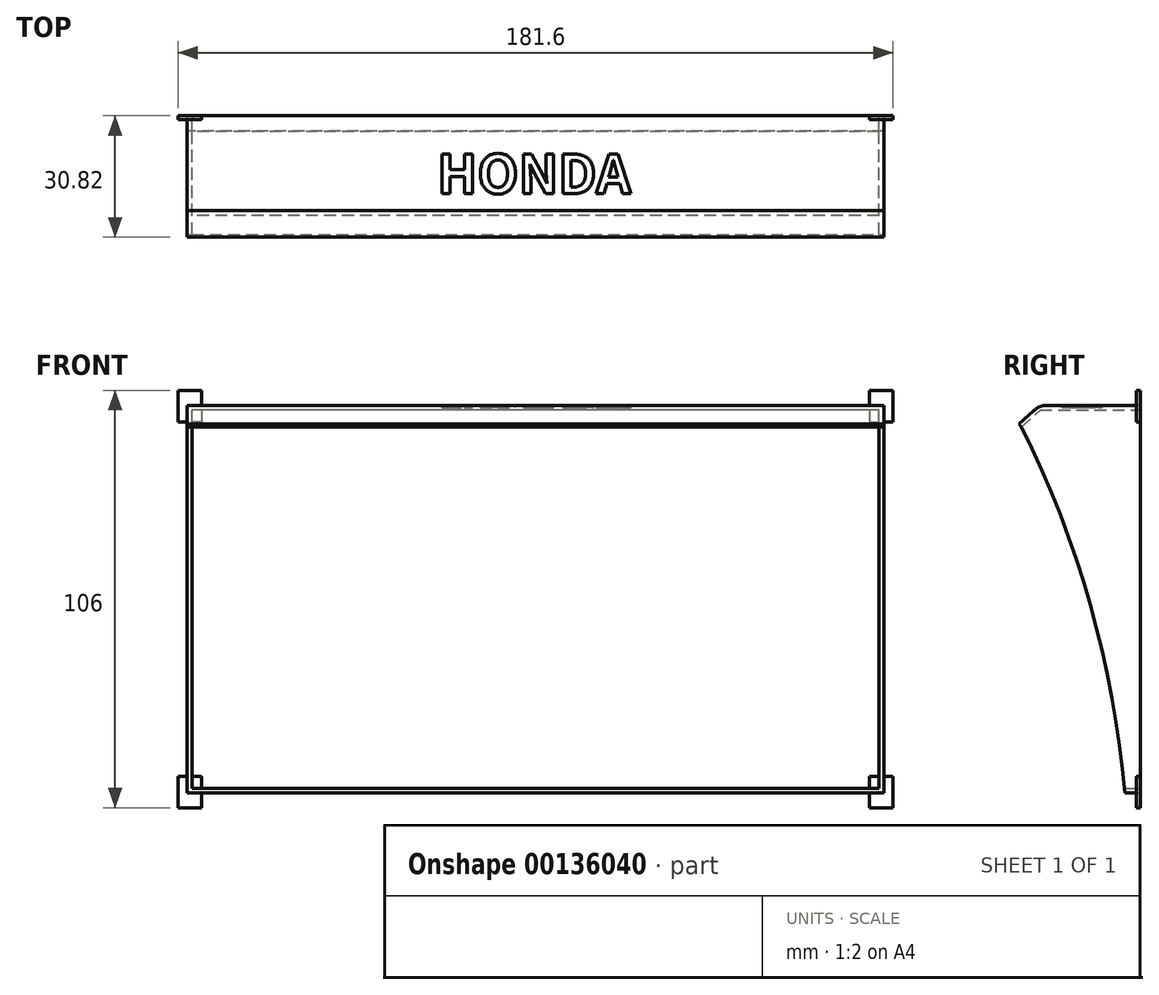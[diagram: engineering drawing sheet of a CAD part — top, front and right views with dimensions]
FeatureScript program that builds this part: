
annotation { "Feature Type Name" : "Feature", "Feature Type Description" : "" }
export const myFeature = defineFeature(function(context is Context, id is Id, definition is map)
    precondition{}
    {
        {
            var Q0;
            Q0=qCreatedBy(makeId("Front.planeOp"),FACE);
            var sketch = newSketch(context, id + "F0", { "sketchPlane" : qUnion([Q0])});
            skLineSegment(sketch, "E0.bottom", {"start": v(88.5, -49.25) * mm, "end": v(-88.5, -49.25) * mm});
            skLineSegment(sketch, "E0.top", {"start": v(88.5, 49.25) * mm, "end": v(-88.5, 49.25) * mm});
            skLineSegment(sketch, "E0.left", {"start": v(88.5, -49.25) * mm, "end": v(88.5, 49.25) * mm});
            skLineSegment(sketch, "E0.right", {"start": v(-88.5, -49.25) * mm, "end": v(-88.5, 49.25) * mm});
            skPoint(sketch, "E0.middle", {"position": v(0, 0) * mm});
            skSolve(sketch);
        }
        {
            var Q0;
            Q0=makeQuery(id+"F0.imprint","IMPRINT",FACE,{"disambiguationData":[TD([[makeQuery(id+"F0.imprint","IMPRINT",EDGE,{"derivedFrom":sQuery(id+"F0.wireOp",EDGE,"E0.bottom")}),-1.0]])]});
            extrude(context, id + "F1", {"entities" : qUnion([Q0]), "depth" : 33 * mm});
        }
        {
            var Q0;
            Q0=makeQuery(id+"F1.opExtrude","CAP_FACE",FACE,{"disambiguationData":[OSD([sQuery(id+"F0.wireOp",EDGE,"E0.bottom"),sQuery(id+"F0.wireOp",EDGE,"E0.top"),sQuery(id+"F0.wireOp",EDGE,"E0.left"),sQuery(id+"F0.wireOp",EDGE,"E0.right")])],"isStart":false});
            var Q1;
            Q1=makeQuery(id+"F1.opExtrude","CAP_FACE",FACE,{"disambiguationData":[OSD([sQuery(id+"F0.wireOp",EDGE,"E0.bottom"),sQuery(id+"F0.wireOp",EDGE,"E0.top"),sQuery(id+"F0.wireOp",EDGE,"E0.left"),sQuery(id+"F0.wireOp",EDGE,"E0.right")])],"isStart":true});
            shell(context, id + "F2", {"entities" : qUnion([Q0, Q1]), "thickness" : 1.2 * mm});
        }
        {
            var Q0;
            Q0=makeQuery(id+"F1.opExtrude","SWEPT_FACE",FACE,{"disambiguationData":[OSD([sQuery(id+"F0.wireOp",EDGE,"E0.right")])]});
            var sketch = newSketch(context, id + "F3", { "sketchPlane" : qUnion([Q0])});
            skArc(sketch, "E1", {"start": v(33, 49.25) * mm, "mid": v(13.5, 1.47) * mm, "end": v(3.94, -49.25) * mm});
            skSolve(sketch);
        }
        {
            var Q0;
            {var subQ0=sQuery(id+"F3.wireOp",EDGE,"E1");Q0=makeQuery(id+"F3.imprint","IMPRINT",FACE,{"disambiguationData":[TD([[makeQuery(id+"F3.imprint","IMPRINT",EDGE,{"derivedFrom":subQ0}),1.0]])]});}
            var Q1;
            Q1=sQuery(id+"F3.wireOp",EDGE,"E1");
            extrude(context, id + "F4", {"entities" : qUnion([Q0]), "operationType" : NewBodyOperationType.REMOVE, "surfaceEntities" : qUnion([Q1]), "endBound" : BoundingType.THROUGH_ALL, "oppositeDirection" : true, "depth" : 25 * mm});
        }
        {
            var Q0;
            Q0=makeQuery(id+"F1.opExtrude","SWEPT_FACE",FACE,{"disambiguationData":[OSD([sQuery(id+"F0.wireOp",EDGE,"E0.top")])]});
            var sketch = newSketch(context, id + "F5", { "sketchPlane" : qUnion([Q0])});
            skText(sketch, "E2", { "text": "HONDA", "fontName": "NotoSansCJKjp-Bold.otf"});
            const initialGuessF5  = {"E2": [-0.025, -0.01975, 1, 0, 0.00975]};
            skSetInitialGuess(sketch, initialGuessF5);
            skSolve(sketch);
        }
        {
            var Q0;
            Q0 = qSketchRegion(id + "F5", true);
            extrude(context, id + "F6", {"entities" : qUnion([Q0]), "operationType" : NewBodyOperationType.REMOVE, "oppositeDirection" : true, "depth" : 0.5 * mm});
        }
        {
            var Q0;
            Q0=qCreatedBy(makeId("Front.planeOp"),FACE);
            var sketch = newSketch(context, id + "F7", { "sketchPlane" : qUnion([Q0])});
            skLineSegment(sketch, "E3.bottom", {"start": v(84.8, 53) * mm, "end": v(90.8, 53) * mm});
            skLineSegment(sketch, "E3.top", {"start": v(84.8, 45) * mm, "end": v(90.8, 45) * mm});
            skLineSegment(sketch, "E3.left", {"start": v(84.8, 53) * mm, "end": v(84.8, 45) * mm});
            skLineSegment(sketch, "E3.right", {"start": v(90.8, 53) * mm, "end": v(90.8, 45) * mm});
            skPoint(sketch, "E3.middle", {"position": v(87.8, 49) * mm});
            skPoint(sketch, "E4.MirrorP", {"position": v(-87.8, 49) * mm});
            skLineSegment(sketch, "E5.MirrorCS", {"start": v(-90.8, 53) * mm, "end": v(-90.8, 45) * mm});
            skLineSegment(sketch, "E6.MirrorCS", {"start": v(-84.8, 53) * mm, "end": v(-90.8, 53) * mm});
            skLineSegment(sketch, "E7.MirrorCS", {"start": v(-84.8, 53) * mm, "end": v(-84.8, 45) * mm});
            skLineSegment(sketch, "E8.MirrorCS", {"start": v(-84.8, 45) * mm, "end": v(-90.8, 45) * mm});
            skLineSegment(sketch, "E9.MirrorCS", {"start": v(84.8, -45) * mm, "end": v(90.8, -45) * mm});
            skLineSegment(sketch, "E10.MirrorCS", {"start": v(84.8, -53) * mm, "end": v(90.8, -53) * mm});
            skLineSegment(sketch, "E11.MirrorCS", {"start": v(84.8, -53) * mm, "end": v(84.8, -45) * mm});
            skLineSegment(sketch, "E12.MirrorCS", {"start": v(90.8, -53) * mm, "end": v(90.8, -45) * mm});
            skLineSegment(sketch, "E13.MirrorCS", {"start": v(-84.8, -53) * mm, "end": v(-84.8, -45) * mm});
            skLineSegment(sketch, "E14.MirrorCS", {"start": v(-84.8, -45) * mm, "end": v(-90.8, -45) * mm});
            skLineSegment(sketch, "E15.MirrorCS", {"start": v(-90.8, -53) * mm, "end": v(-90.8, -45) * mm});
            skLineSegment(sketch, "E16.MirrorCS", {"start": v(-84.8, -53) * mm, "end": v(-90.8, -53) * mm});
            skSolve(sketch);
        }
        {
            var Q0;
            Q0 = qSketchRegion(id + "F7", true);
            extrude(context, id + "F8", {"entities" : qUnion([Q0]), "operationType" : NewBodyOperationType.ADD, "depth" : 1 * mm});
        }
        {
            var Q0;
            Q0=makeQuery(id+"F1.opExtrude","SWEPT_FACE",FACE,{"disambiguationData":[OSD([sQuery(id+"F0.wireOp",EDGE,"E0.left")])]});
            var sketch = newSketch(context, id + "F9", { "sketchPlane" : qUnion([Q0])});
            skLineSegment(sketch, "E17", {"start": v(-24.05, 49.25) * mm, "end": v(-30.14, 43.71) * mm});
            skSolve(sketch);
        }
        {
            var Q0;
            Q0 = qSketchRegion(id + "F9", true);
            var Q1;
            {var subQ0=sQuery(id+"F9.wireOp",EDGE,"E17");Q1=makeQuery(id+"F9.imprint","IMPRINT",FACE,{"disambiguationData":[TD([[makeQuery(id+"F9.imprint","IMPRINT",EDGE,{"derivedFrom":subQ0}),-1.0]])]});}
            extrude(context, id + "F10", {"entities" : qUnion([Q0, Q1]), "operationType" : NewBodyOperationType.REMOVE, "endBound" : BoundingType.THROUGH_ALL, "oppositeDirection" : true, "depth" : 25 * mm});
        }
        {
            var Q0;
            Q0=makeQuery(id+"F10.boolean.opBoolean","COPY",FACE,{"derivedFrom":makeQuery(id+"F10.opExtrude","SWEPT_FACE",FACE,{"disambiguationData":[OSD([sQuery(id+"F9.wireOp",EDGE,"E17")])]})});
            var sketch = newSketch(context, id + "F11", { "sketchPlane" : qUnion([Q0])});
            skLineSegment(sketch, "E18.bottom", {"start": v(-88.5, 15.3) * mm, "end": v(88.5, 15.3) * mm});
            skLineSegment(sketch, "E18.top", {"start": v(-88.5, 7.07) * mm, "end": v(88.5, 7.07) * mm});
            skLineSegment(sketch, "E18.left", {"start": v(-88.5, 15.3) * mm, "end": v(-88.5, 7.07) * mm});
            skLineSegment(sketch, "E18.right", {"start": v(88.5, 15.3) * mm, "end": v(88.5, 7.07) * mm});
            skSolve(sketch);
        }
        {
            var Q0;
            Q0 = qSketchRegion(id + "F11", true);
            extrude(context, id + "F12", {"entities" : qUnion([Q0]), "operationType" : NewBodyOperationType.ADD, "depth" : 1 * mm});
        }
        {
            var Q0;
            Q0=makeQuery(id+"F12.opExtrude","CAP_EDGE",EDGE,{"disambiguationData":[OSD([sQuery(id+"F11.wireOp",EDGE,"E18.bottom")])],"isStart":false});
            fillet(context, id + "F13", {"entities" : qUnion([Q0]), "radius" : 5 * mm, "tangentPropagation" : true, "allowEdgeOverflow" : false});
        }
    });
